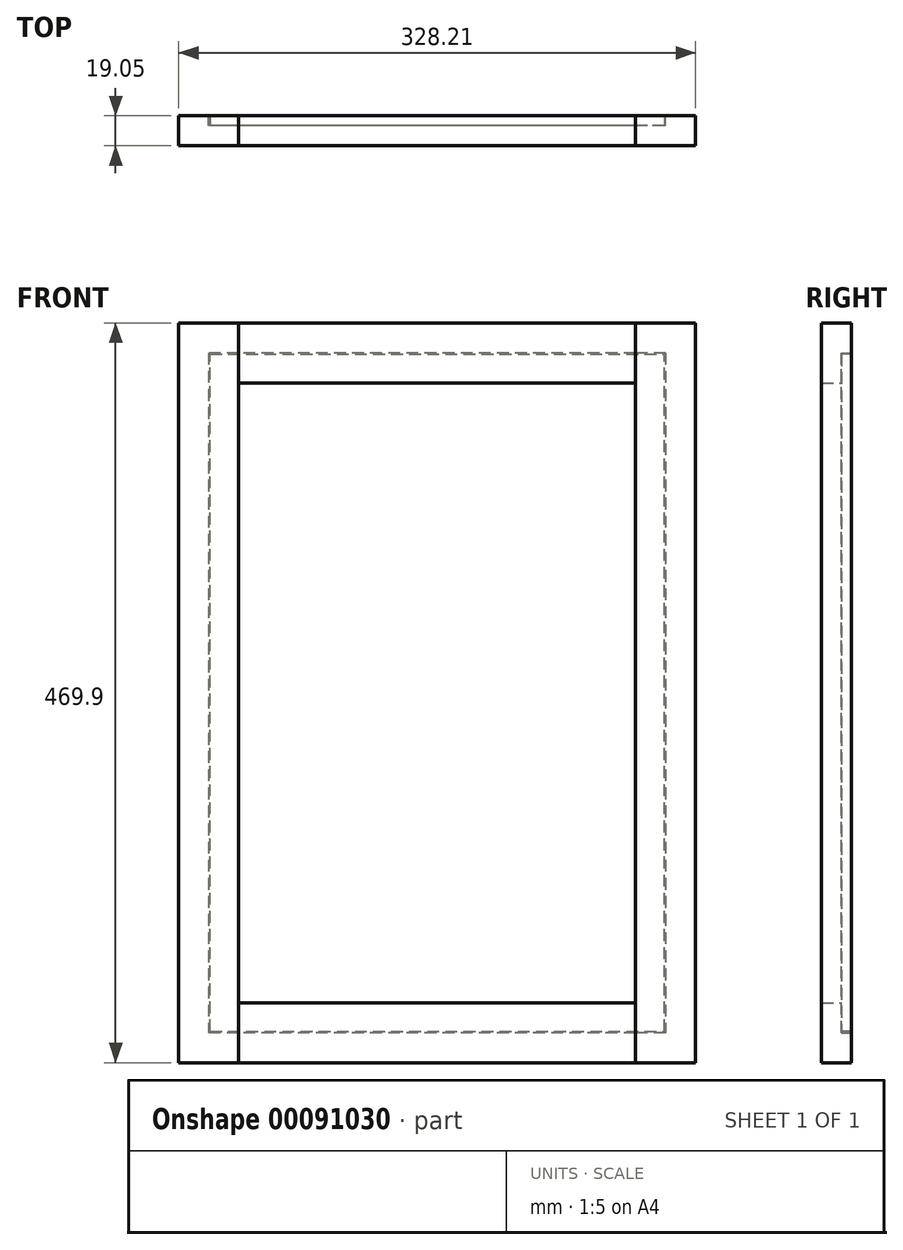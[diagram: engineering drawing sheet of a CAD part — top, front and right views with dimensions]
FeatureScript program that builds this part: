
annotation { "Feature Type Name" : "Feature", "Feature Type Description" : "" }
export const myFeature = defineFeature(function(context is Context, id is Id, definition is map)
    precondition{}
    {
        {
            var Q0;
            Q0=qCreatedBy(makeId("Front.planeOp"),FACE);
            var sketch = newSketch(context, id + "F0", { "sketchPlane" : qUnion([Q0])});
            skLineSegment(sketch, "E0.bottom", {"start": v(0, 0) * mm, "end": v(-328.2, 0) * mm});
            skLineSegment(sketch, "E0.top", {"start": v(0, 469.9) * mm, "end": v(-328.2, 469.9) * mm});
            skLineSegment(sketch, "E0.left", {"start": v(0, 0) * mm, "end": v(0, 469.9) * mm});
            skLineSegment(sketch, "E0.right", {"start": v(-328.2, 0) * mm, "end": v(-328.2, 469.9) * mm});
            skLineSegment(sketch, "E1", {"start": v(-290.1, 469.9) * mm, "end": v(-290.1, 0) * mm});
            skLineSegment(sketch, "E2", {"start": v(-38.1, 469.9) * mm, "end": v(-38.1, 0) * mm});
            skLineSegment(sketch, "E3", {"start": v(-290.1, 431.8) * mm, "end": v(-38.1, 431.8) * mm});
            skLineSegment(sketch, "E4", {"start": v(-290.1, 38.1) * mm, "end": v(-38.1, 38.1) * mm});
            skSolve(sketch);
        }
        {
            var Q0;
            {var subQ5=sQuery(id+"F0.wireOp",EDGE,"E3");Q0=makeQuery(id+"F0.imprint","IMPRINT",FACE,{"disambiguationData":[TD([[makeQuery(id+"F0.imprint","IMPRINT",EDGE,{"derivedFrom":subQ5}),1.0]])]});}
            extrude(context, id + "F1", {"entities" : qUnion([Q0]), "depth" : 19.05 * mm});
        }
        {
            var Q0;
            {var subQ4=sQuery(id+"F0.wireOp",EDGE,"E0.right");Q0=makeQuery(id+"F0.imprint","IMPRINT",FACE,{"disambiguationData":[TD([[makeQuery(id+"F0.imprint","IMPRINT",EDGE,{"derivedFrom":subQ4}),-1.0]])]});}
            extrude(context, id + "F2", {"entities" : qUnion([Q0]), "depth" : 19.05 * mm});
        }
        {
            var Q0;
            {var subQ5=sQuery(id+"F0.wireOp",EDGE,"E4");Q0=makeQuery(id+"F0.imprint","IMPRINT",FACE,{"disambiguationData":[TD([[makeQuery(id+"F0.imprint","IMPRINT",EDGE,{"derivedFrom":subQ5}),-1.0]])]});}
            extrude(context, id + "F3", {"entities" : qUnion([Q0]), "depth" : 19.05 * mm});
        }
        {
            var Q0;
            {var subQ4=sQuery(id+"F0.wireOp",EDGE,"E0.left");Q0=makeQuery(id+"F0.imprint","IMPRINT",FACE,{"disambiguationData":[TD([[makeQuery(id+"F0.imprint","IMPRINT",EDGE,{"derivedFrom":subQ4}),1.0]])]});}
            extrude(context, id + "F4", {"entities" : qUnion([Q0]), "depth" : 19.05 * mm});
        }
        {
            var Q0;
            Q0=makeQuery(id+"F1.opExtrude","CAP_FACE",FACE,{"disambiguationData":[OSD([sQuery(id+"F0.wireOp",EDGE,"E0.top"),sQuery(id+"F0.wireOp",EDGE,"E1"),sQuery(id+"F0.wireOp",EDGE,"E2"),sQuery(id+"F0.wireOp",EDGE,"E3")])],"isStart":true});
            var sketch = newSketch(context, id + "F5", { "sketchPlane" : qUnion([Q0])});
            skLineSegment(sketch, "E5.bottom", {"start": v(19.05, 450.85) * mm, "end": v(309.16, 450.85) * mm});
            skLineSegment(sketch, "E5.top", {"start": v(19.05, 19.05) * mm, "end": v(309.16, 19.05) * mm});
            skLineSegment(sketch, "E5.left", {"start": v(19.05, 450.85) * mm, "end": v(19.05, 19.05) * mm});
            skLineSegment(sketch, "E5.right", {"start": v(309.16, 450.85) * mm, "end": v(309.16, 19.05) * mm});
            skSolve(sketch);
        }
        {
            var Q0;
            Q0=makeQuery(id+"F5.imprint","IMPRINT",FACE,{"disambiguationData":[TD([[makeQuery(id+"F5.imprint","IMPRINT",EDGE,{"derivedFrom":sQuery(id+"F5.wireOp",EDGE,"E5.top")}),1.0]])]});
            var Q1;
            {var subQ5=makeQuery(id+"F1.opExtrude","CAP_EDGE",EDGE,{"disambiguationData":[OSD([sQuery(id+"F0.wireOp",EDGE,"E3")])],"isStart":true});Q1=makeQuery(id+"F5.imprint","IMPRINT",FACE,{"disambiguationData":[TD([[makeQuery(id+"F5.imprint","IMPRINT",EDGE,{"derivedFrom":subQ5}),-1.0]])]});}
            extrude(context, id + "F6", {"entities" : qUnion([Q0, Q1]), "operationType" : NewBodyOperationType.REMOVE, "oppositeDirection" : true, "depth" : 6.35 * mm});
        }
        {
            var Q0;
            Q0=makeQuery(id+"F6.boolean.opBoolean","COPY",FACE,{"disambiguationData":[OD(2.0)],"derivedFrom":makeQuery(id+"F6.opExtrude","CAP_FACE",FACE,{"disambiguationData":[OSD([sQuery(id+"F5.wireOp",EDGE,"E5.bottom"),sQuery(id+"F5.wireOp",EDGE,"E5.top"),sQuery(id+"F5.wireOp",EDGE,"E5.left"),sQuery(id+"F5.wireOp",EDGE,"E5.right")])],"isStart":false})});
            var sketch = newSketch(context, id + "F7", { "sketchPlane" : qUnion([Q0])});
            skLineSegment(sketch, "E6.bottom", {"start": v(19.86, 450.04) * mm, "end": v(308.34, 450.04) * mm});
            skLineSegment(sketch, "E6.top", {"start": v(19.86, 19.86) * mm, "end": v(308.34, 19.86) * mm});
            skLineSegment(sketch, "E6.left", {"start": v(19.86, 450.04) * mm, "end": v(19.86, 19.86) * mm});
            skLineSegment(sketch, "E6.right", {"start": v(308.34, 450.04) * mm, "end": v(308.34, 19.86) * mm});
            skSolve(sketch);
        }
        {
            var Q0;
            Q0 = qSketchRegion(id + "F7", true);
            var Q1;
            Q1=makeQuery(id+"F1.opExtrude","CAP_FACE",FACE,{"disambiguationData":[OSD([sQuery(id+"F0.wireOp",EDGE,"E0.top"),sQuery(id+"F0.wireOp",EDGE,"E1"),sQuery(id+"F0.wireOp",EDGE,"E2"),sQuery(id+"F0.wireOp",EDGE,"E3")])],"isStart":true});
            extrude(context, id + "F8", {"entities" : qUnion([Q0]), "endBound" : BoundingType.UP_TO_SURFACE, "endBoundEntityFace" : qUnion([Q1]), "depth" : 6.35 * mm});
        }
    });
